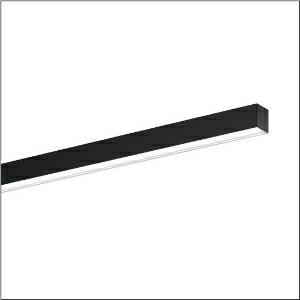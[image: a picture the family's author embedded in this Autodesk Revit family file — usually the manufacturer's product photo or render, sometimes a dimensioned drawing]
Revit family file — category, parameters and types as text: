
# Revit family: silica_r__21_51mx23tat4b_8a74
name_source: partatom
category: Lighting Fixtures
units: mm (PartAtom-declared; Revit-internal decimal feet)

## family parameters
Cut with Voids When Loaded = No
Host = Face
Light Source = No
Part Type = Normal
Room Calculation Point = No
Round Connector Dimension = Use Diameter
Shared = No

## types (1)
- --- (1 x LED, 3230 lm, 32.4 W, 6500K)
    Apparent Load = 32 VA
    CIE Flux Codes = 78 96 99 100 100
    Color Rendering = 80
    Color Temperature = 6500K
    Default Elevation = 1800 mm
    Description = Silica® 21, office luminaire, primary optical cover: prismatic diffuser, of PMMA, CAT 2 (L<= 3000cd/m²), light emission: direct distribution, primary light characteristic: symmetric, installation type: surface-mounted, LED, rated luminous flux: 3.230lm, luminous efficacy: 95lm/W, light colour: 8tw, colour temperature: 2700..6500K, control gear: DALI DT8, with terminal, 3+2-pole, max. 2.5mm², mains connection: 220..240V, AC, 50/60Hz, rated input power: 34W, luminaire housing, of aluminium, matt jet black (RAL 9005), length: 1.204mm, width: 53mm, height: 53mm, protection rating (complete): IP20, insulation class (complete): insulation class I (protective earthing), certification: CE, permissible operating ambient temperature: 0..+35°C, standard: EN 50419, packaging unit: 1 piece
    Height = 53 mm
    Lamp = 1 x LED
    Lamp Light Flux = 3230 lm
    Lamp Power = 32.4 W
    Lamp count = 1
    Length = 1204 mm
    Luminous efficacy = 100 lm/W
    Manufacturer = Siteco
    ModVariant = No
    Model = 51MX23TAT4B
    Mounting Place = Ceiling
    Mounting Type = Surface mounted
    Number of Poles = 1
    OnlyDefault = Yes
    Power Factor = 1
    Product Name = Silica® 21
    Product group = office luminaire | ceiling mounted
    ProductGroupID = 302
    Protection Class = Protection class I
    Protection Degree = IP 20
    RLX_Detail_Level = 1
    RLX_Emergency_Light_Flux = 0 lm
    RLX_Emergency_Type = 0
    RLX_Emergency_Type_DB = No
    RlxData = <blob elided: 20473 chars, md5=4d1f9c47>
    Socket = socket
    Standby Power = 0 W
    System Light Flux = 3230 lm
    System Power = 32 W
    Type Comments = individual setting
    Type Image = l_1335925.jpg
    URL = http://relux.com
    VarID = @adj_139818
    Voltage = 0 V
    Weight = 0.00 kg
    Width = 53 mm

## geometry (parser evidence)
native form markers: Blend x4, Sweep x9
no freeform markers — native parametric forms only
